# Revit family: Electrical-Teknion-JNEPC_Power_Cube-R2015
name_source: partatom
category: Electrical Fixtures
revit_build: Autodesk Revit Architecture 2015 (Build: 20140323_1530(x64)
units: mm (PartAtom-declared; Revit-internal decimal feet)

## types (3) — shared parameters
Apparent Load = 0 VA
Connector Descriptor = Power Connector
Default Elevation = 4' - 0"
Description = Power Cube
Has Power Cube Above Worksurface = Yes
Has Power Cube Below Worksurface = No
Manufacturer = Teknion
Manufacturer Fax = 416.661.4586
Model = JNEPC
Part Number = JNEPC
Product Documentation Link = http://www.teknion.com
Product Line = Expansion Cityline
Product Page URL = http://www.teknion.com
Series = Expansion Cityline
Sustainability Data = http://www.teknion.com
URL = www.teknion.com
Unit Weight URL = http://www.teknion.com
Voltage = 120 V
Warranty = http://www.teknion.com

## per-type parameters (varying)
| type | Has Power & Power slot | Has Power & USB Charger slot | Has Quad - 2 Power/2 USB/1 Data |
| Dual - Power Only | Yes | No | No |
| Dual - 1 Power / 2 USB / 0 Data | No | Yes | No |
| Quad - 2 Power/ 2 USB/1 Data | No | No | Yes |

## geometry (parser evidence)
native form markers: Blend x6, Sweep x2
no freeform markers — native parametric forms only
